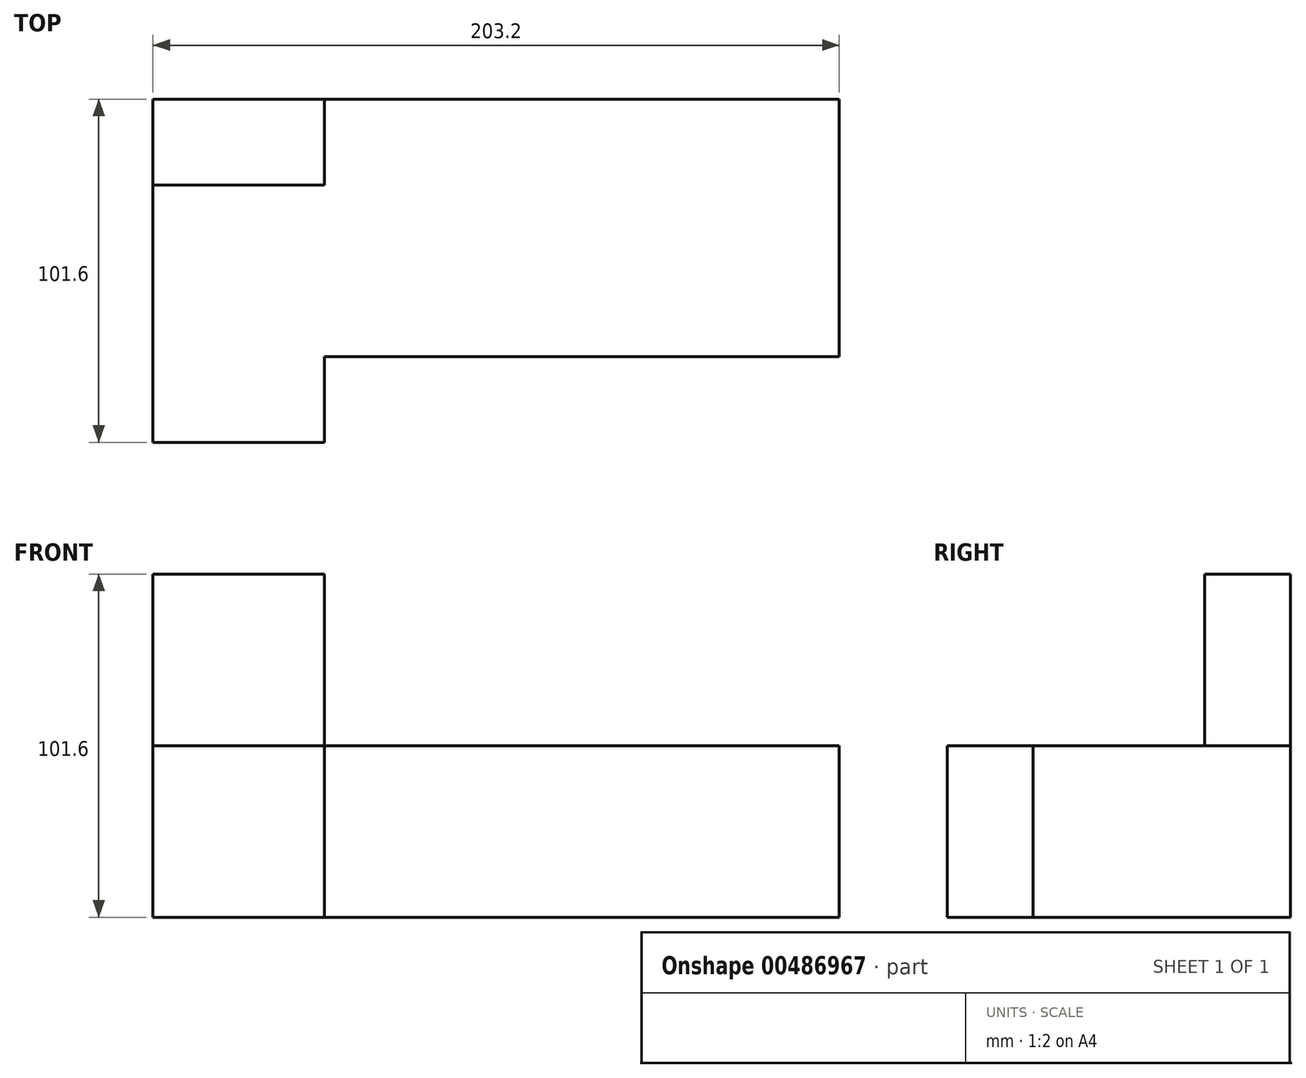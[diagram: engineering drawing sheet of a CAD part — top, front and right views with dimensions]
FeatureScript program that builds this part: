
annotation { "Feature Type Name" : "Feature", "Feature Type Description" : "" }
export const myFeature = defineFeature(function(context is Context, id is Id, definition is map)
    precondition{}
    {
        {
            var Q0;
            Q0=qCreatedBy(makeId("Front.planeOp"),FACE);
            var sketch = newSketch(context, id + "F0", { "sketchPlane" : qUnion([Q0])});
            skLineSegment(sketch, "E0.bottom", {"start": v(0, 0) * mm, "end": v(-152.4, 0) * mm});
            skLineSegment(sketch, "E0.top", {"start": v(0, 76.2) * mm, "end": v(-203.2, 76.2) * mm});
            skLineSegment(sketch, "E0.left", {"start": v(0, 0) * mm, "end": v(0, 76.2) * mm});
            skLineSegment(sketch, "E0.right", {"start": v(-203.2, 0) * mm, "end": v(-203.2, 76.2) * mm});
            skLineSegment(sketch, "E1.top", {"start": v(-203.2, -25.4) * mm, "end": v(-152.4, -25.4) * mm});
            skLineSegment(sketch, "E1.left", {"start": v(-203.2, 0) * mm, "end": v(-203.2, -25.4) * mm});
            skLineSegment(sketch, "E1.right", {"start": v(-152.4, 0) * mm, "end": v(-152.4, -25.4) * mm});
            skSolve(sketch);
        }
        {
            var Q0;
            Q0=makeQuery(id+"F0.imprint","IMPRINT",FACE,{"disambiguationData":[TD([[makeQuery(id+"F0.imprint","IMPRINT",EDGE,{"derivedFrom":sQuery(id+"F0.wireOp",EDGE,"E0.bottom")}),-1.0]])]});
            extrude(context, id + "F1", {"entities" : qUnion([Q0]), "depth" : 50.8 * mm});
        }
        {
            var Q0;
            Q0=makeQuery(id+"F1.opExtrude","CAP_FACE",FACE,{"disambiguationData":[OSD([sQuery(id+"F0.wireOp",EDGE,"E0.bottom"),sQuery(id+"F0.wireOp",EDGE,"E0.top"),sQuery(id+"F0.wireOp",EDGE,"E0.left"),sQuery(id+"F0.wireOp",EDGE,"E0.right"),sQuery(id+"F0.wireOp",EDGE,"E1.top"),sQuery(id+"F0.wireOp",EDGE,"E1.left"),sQuery(id+"F0.wireOp",EDGE,"E1.right")])],"isStart":false});
            var sketch = newSketch(context, id + "F2", { "sketchPlane" : qUnion([Q0])});
            skLineSegment(sketch, "E2.bottom", {"start": v(-203.2, 76.2) * mm, "end": v(-152.4, 76.2) * mm});
            skLineSegment(sketch, "E2.top", {"start": v(-203.2, 50.8) * mm, "end": v(-152.4, 50.8) * mm});
            skLineSegment(sketch, "E2.left", {"start": v(-203.2, 76.2) * mm, "end": v(-203.2, 50.8) * mm});
            skLineSegment(sketch, "E2.right", {"start": v(-152.4, 76.2) * mm, "end": v(-152.4, 50.8) * mm});
            skSolve(sketch);
        }
        {
            var Q0;
            Q0=makeQuery(id+"F2.imprint","IMPRINT",FACE,{"disambiguationData":[TD([[makeQuery(id+"F2.imprint","IMPRINT",EDGE,{"derivedFrom":sQuery(id+"F2.wireOp",EDGE,"E2.bottom")}),1.0]])]});
            extrude(context, id + "F3", {"entities" : qUnion([Q0]), "operationType" : NewBodyOperationType.ADD, "depth" : 50.8 * mm});
        }
        {
            var Q0;
            Q0=makeQuery(id+"F1.opExtrude","SWEPT_BODY",BODY,{"disambiguationData":[OSD([sQuery(id+"F0.wireOp",EDGE,"E0.bottom"),sQuery(id+"F0.wireOp",EDGE,"E0.top"),sQuery(id+"F0.wireOp",EDGE,"E0.left"),sQuery(id+"F0.wireOp",EDGE,"E0.right"),sQuery(id+"F0.wireOp",EDGE,"E1.top"),sQuery(id+"F0.wireOp",EDGE,"E1.left"),sQuery(id+"F0.wireOp",EDGE,"E1.right")])]});
            var Q1;
            Q1=makeQuery(id+"F1.opExtrude","CAP_EDGE",EDGE,{"disambiguationData":[OSD([sQuery(id+"F0.wireOp",EDGE,"E0.top")])],"isStart":true});
            transform(context, id + "F4", {"entities" : qUnion([Q0]), "transformType" : TransformType.ROTATION, "transformAxis" : qUnion([Q1]), "angle" : 90 * degree, "makeCopy" : false});
        }
    });
